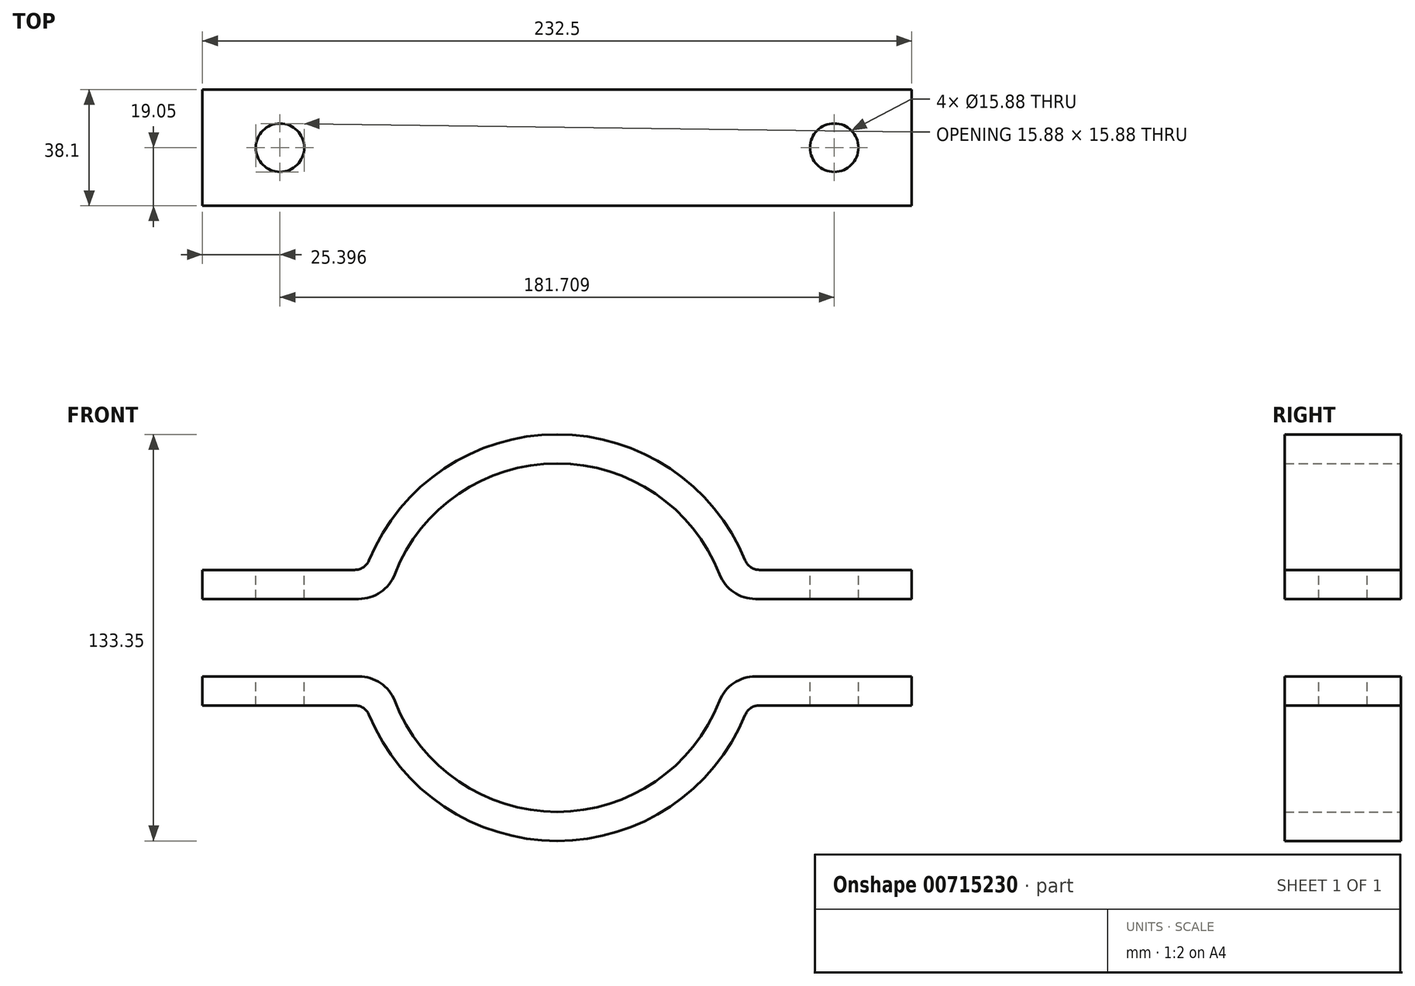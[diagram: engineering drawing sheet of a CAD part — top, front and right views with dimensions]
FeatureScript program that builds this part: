
annotation { "Feature Type Name" : "Feature", "Feature Type Description" : "" }
export const myFeature = defineFeature(function(context is Context, id is Id, definition is map)
    precondition{}
    {
        {
            var Q0;
            Q0=qCreatedBy(makeId("Front.planeOp"),FACE);
            var sketch = newSketch(context, id + "F0", { "sketchPlane" : qUnion([Q0])});
            skArc(sketch, "E0", {"start": v(-55.72, -12.7) * mm, "mid": v(0, -57.15) * mm, "end": v(55.72, -12.7) * mm});
            skArc(sketch, "E1", {"start": v(-62.86, -22.23) * mm, "mid": v(0, -66.68) * mm, "end": v(62.86, -22.23) * mm});
            skLineSegment(sketch, "E2", {"start": v(-65.45, 12.7) * mm, "end": v(-116.25, 12.7) * mm});
            skLineSegment(sketch, "E3.MirrorCS", {"start": v(-65.45, -12.7) * mm, "end": v(-116.25, -12.7) * mm});
            skLineSegment(sketch, "E4.MirrorCS", {"start": v(65.45, -12.7) * mm, "end": v(116.25, -12.7) * mm});
            skLineSegment(sketch, "E5.MirrorCS", {"start": v(65.45, 12.7) * mm, "end": v(116.25, 12.7) * mm});
            skLineSegment(sketch, "E6", {"start": v(-116.25, 12.7) * mm, "end": v(-116.25, 22.22) * mm});
            skLineSegment(sketch, "E7", {"start": v(-116.25, 22.22) * mm, "end": v(-62.86, 22.22) * mm});
            skLineSegment(sketch, "E8", {"start": v(-116.25, -12.7) * mm, "end": v(-116.25, -22.23) * mm});
            skLineSegment(sketch, "E9", {"start": v(-116.25, -22.23) * mm, "end": v(-62.86, -22.23) * mm});
            skLineSegment(sketch, "E10.MirrorCS", {"start": v(116.25, 12.7) * mm, "end": v(116.25, 22.22) * mm});
            skLineSegment(sketch, "E11.MirrorCS", {"start": v(116.25, 22.22) * mm, "end": v(62.86, 22.22) * mm});
            skLineSegment(sketch, "E12.MirrorCS", {"start": v(116.25, -22.23) * mm, "end": v(62.86, -22.23) * mm});
            skLineSegment(sketch, "E13.MirrorCS", {"start": v(116.25, -12.7) * mm, "end": v(116.25, -22.23) * mm});
            skLineSegment(sketch, "E14", {"start": v(-65.45, 12.7) * mm, "end": v(-55.72, 12.7) * mm});
            skLineSegment(sketch, "E15.MirrorCS", {"start": v(-65.45, -12.7) * mm, "end": v(-55.72, -12.7) * mm});
            skLineSegment(sketch, "E16.MirrorCS", {"start": v(65.45, 12.7) * mm, "end": v(55.72, 12.7) * mm});
            skLineSegment(sketch, "E17.MirrorCS", {"start": v(65.45, -12.7) * mm, "end": v(55.72, -12.7) * mm});
            skArc(sketch, "E18.trimOffspring", {"start": v(62.86, 22.22) * mm, "mid": v(0, 66.68) * mm, "end": v(-62.86, 22.23) * mm});
            skArc(sketch, "E19.trimOffspring", {"start": v(55.72, 12.7) * mm, "mid": v(0, 57.15) * mm, "end": v(-55.72, 12.7) * mm});
            skSolve(sketch);
        }
        {
            var Q0;
            Q0 = qSketchRegion(id + "F0", true);
            extrude(context, id + "F1", {"entities" : qUnion([Q0]), "endBound" : BoundingType.SYMMETRIC, "depth" : 38.1 * mm, "offsetDistance" : 25.4 * mm});
        }
        {
            var Q0;
            Q0=makeQuery(id+"F1.opExtrude","SWEPT_EDGE",EDGE,{"disambiguationData":[OSD([sQuery(id+"F0.wireOp",EDGE,"E7"),sQuery(id+"F0.wireOp",EDGE,"E18.trimOffspring")])]});
            var Q1;
            Q1=makeQuery(id+"F1.opExtrude","SWEPT_EDGE",EDGE,{"disambiguationData":[OSD([sQuery(id+"F0.wireOp",EDGE,"E11.MirrorCS"),sQuery(id+"F0.wireOp",EDGE,"E18.trimOffspring")])]});
            var Q2;
            Q2=makeQuery(id+"F1.opExtrude","SWEPT_EDGE",EDGE,{"disambiguationData":[OSD([sQuery(id+"F0.wireOp",EDGE,"E1"),sQuery(id+"F0.wireOp",EDGE,"E12.MirrorCS")])]});
            var Q3;
            Q3=makeQuery(id+"F1.opExtrude","SWEPT_EDGE",EDGE,{"disambiguationData":[OSD([sQuery(id+"F0.wireOp",EDGE,"E1"),sQuery(id+"F0.wireOp",EDGE,"E9")])]});
            fillet(context, id + "F2", {"entities" : qUnion([Q0, Q1, Q2, Q3]), "radius" : 5.08 * mm, "tangentPropagation" : true, "allowEdgeOverflow" : false});
        }
        {
            var Q0;
            Q0=makeQuery(id+"F1.opExtrude","SWEPT_EDGE",EDGE,{"disambiguationData":[OSD([sQuery(id+"F0.wireOp",EDGE,"E14"),sQuery(id+"F0.wireOp",EDGE,"E19.trimOffspring")])]});
            var Q1;
            Q1=makeQuery(id+"F1.opExtrude","SWEPT_EDGE",EDGE,{"disambiguationData":[OSD([sQuery(id+"F0.wireOp",EDGE,"E16.MirrorCS"),sQuery(id+"F0.wireOp",EDGE,"E19.trimOffspring")])]});
            var Q2;
            Q2=makeQuery(id+"F1.opExtrude","SWEPT_EDGE",EDGE,{"disambiguationData":[OSD([sQuery(id+"F0.wireOp",EDGE,"E0"),sQuery(id+"F0.wireOp",EDGE,"E17.MirrorCS")])]});
            var Q3;
            Q3=makeQuery(id+"F1.opExtrude","SWEPT_EDGE",EDGE,{"disambiguationData":[OSD([sQuery(id+"F0.wireOp",EDGE,"E0"),sQuery(id+"F0.wireOp",EDGE,"E15.MirrorCS")])]});
            fillet(context, id + "F3", {"entities" : qUnion([Q0, Q1, Q2, Q3]), "radius" : 12.7 * mm, "tangentPropagation" : true, "allowEdgeOverflow" : false});
        }
        {
            var Q0;
            Q0=makeQuery(id+"F1.opExtrude","SWEPT_FACE",FACE,{"disambiguationData":[OSD([sQuery(id+"F0.wireOp",EDGE,"E7")])]});
            var sketch = newSketch(context, id + "F4", { "sketchPlane" : qUnion([Q0])});
            skCircle(sketch, "E20", {"center": v(-90.85, 0) * mm, "radius": 7.94 * mm});
            skCircle(sketch, "E21.MirrorC", {"center": v(90.85, 0) * mm, "radius": 7.94 * mm});
            skSolve(sketch);
        }
        {
            var Q0;
            Q0 = qSketchRegion(id + "F4", true);
            extrude(context, id + "F5", {"entities" : qUnion([Q0]), "operationType" : NewBodyOperationType.REMOVE, "endBound" : BoundingType.SYMMETRIC, "oppositeDirection" : true, "depth" : 101.6 * mm, "offsetDistance" : 25.4 * mm});
        }
        {
            var Q0;
            Q0=makeQuery(id+"F1.opExtrude","SWEPT_FACE",FACE,{"disambiguationData":[OSD([sQuery(id+"F0.wireOp",EDGE,"E12.MirrorCS")])]});
            var sketch = newSketch(context, id + "F6", { "sketchPlane" : qUnion([Q0])});
            skCircle(sketch, "E22", {"center": v(90.85, 0) * mm, "radius": 7.94 * mm});
            skCircle(sketch, "E23.MirrorC", {"center": v(-90.85, 0) * mm, "radius": 7.94 * mm});
            skSolve(sketch);
        }
        {
            var Q0;
            Q0 = qSketchRegion(id + "F6", true);
            extrude(context, id + "F7", {"entities" : qUnion([Q0]), "operationType" : NewBodyOperationType.REMOVE, "oppositeDirection" : true, "depth" : 25.4 * mm, "offsetDistance" : 25.4 * mm});
        }
    });
